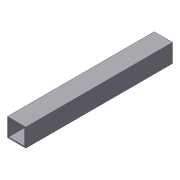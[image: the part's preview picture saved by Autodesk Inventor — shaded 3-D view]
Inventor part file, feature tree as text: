
AUTODESK INVENTOR PART (.ipt)
format: ipt  version: 2012 (Build 160160000, 160)  size: 71,168 bytes
history: native  units: in
note: dims shown in document units (in); Inventor stores cm internally (conversion verified against a paired STEP export)
features: extrude x1, shell x1, sketch x1
ambient origin geometry x8: Origin, YZ Plane, XZ Plane, XY Plane, X Axis, Y Axis, Z Axis, Center Point
bodies: Solid1 (feature_tree)
feature tree (3):
  extrude  "Extrusion1"  Depth=1.0in
  shell  "Shell1"  Thickness=8.0in
  sketch  "Sketch1"  dims[d0=1.0in d1=1.0in d2=8.0in d3=0.0in d4=0.0625in]
